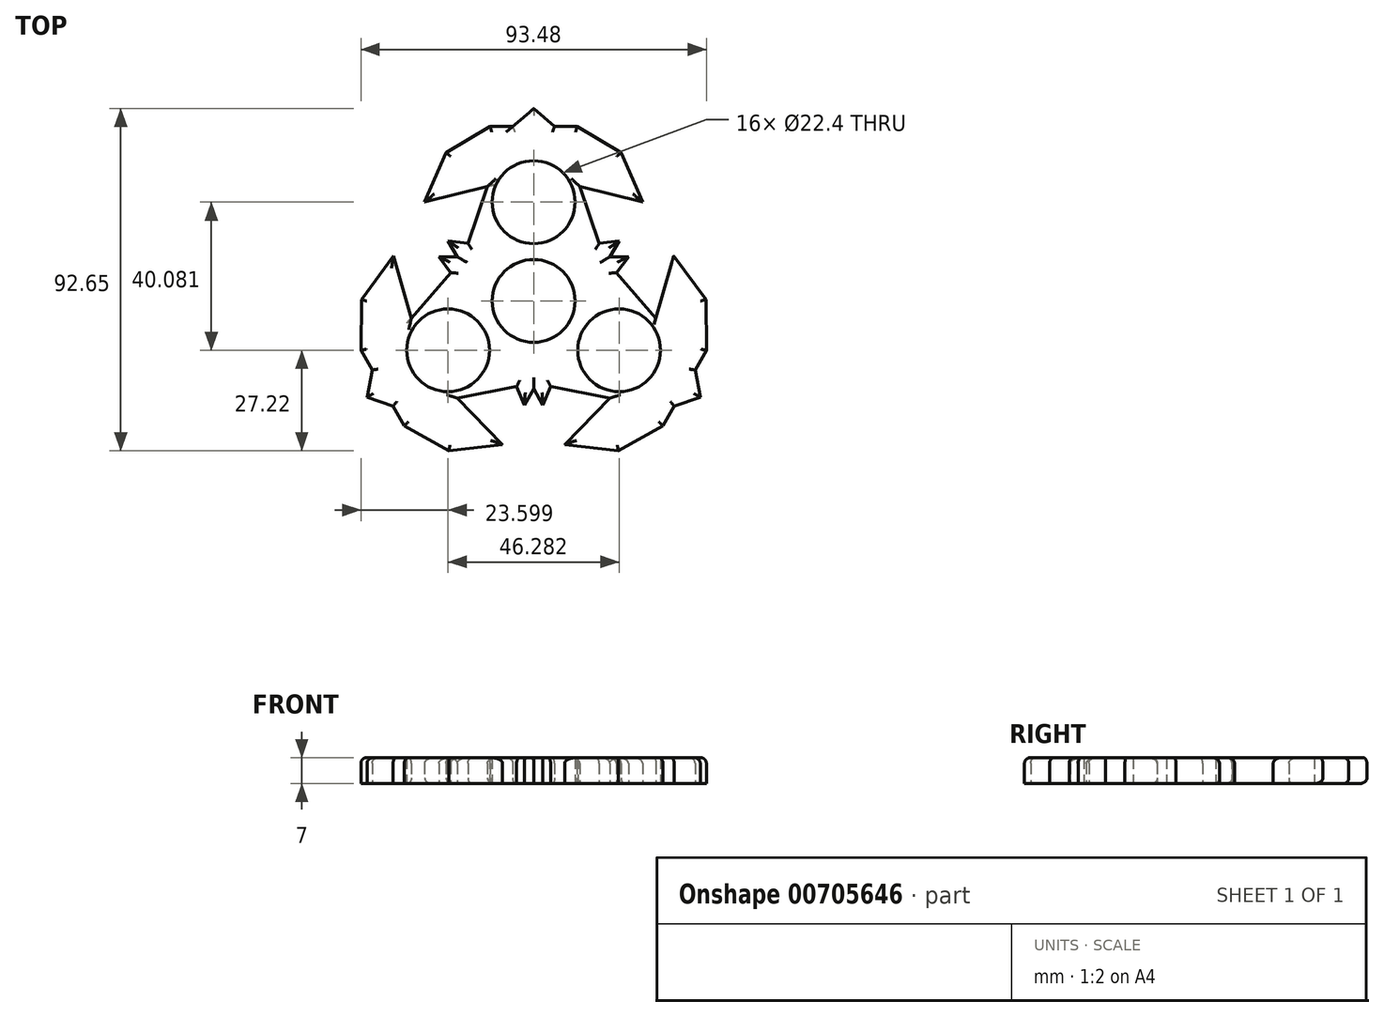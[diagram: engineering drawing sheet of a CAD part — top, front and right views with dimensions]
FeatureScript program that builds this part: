
annotation { "Feature Type Name" : "Feature", "Feature Type Description" : "" }
export const myFeature = defineFeature(function(context is Context, id is Id, definition is map)
    precondition{}
    {
        {
            var Q0;
            Q0=qCreatedBy(makeId("Top.planeOp"),FACE);
            var sketch = newSketch(context, id + "F0", { "sketchPlane" : qUnion([Q0])});
            skCircle(sketch, "E0", {"center": v(0, 0) * mm, "radius": 11.2 * mm});
            skCircle(sketch, "E1", {"center": v(0, 26.72) * mm, "radius": 11.2 * mm});
            skLineSegment(sketch, "E2", {"start": v(-12.5, 30.98) * mm, "end": v(-29.47, 26.72) * mm});
            skLineSegment(sketch, "E3", {"start": v(-29.47, 26.72) * mm, "end": v(-23.67, 40.16) * mm});
            skLineSegment(sketch, "E4", {"start": v(-23.67, 40.16) * mm, "end": v(-11.76, 47.18) * mm});
            skLineSegment(sketch, "E5", {"start": v(-11.76, 47.18) * mm, "end": v(-5.65, 47.18) * mm});
            skLineSegment(sketch, "E6", {"start": v(-5.65, 47.18) * mm, "end": v(0, 52.07) * mm});
            skLineSegment(sketch, "E7.MirrorCS", {"start": v(5.65, 47.18) * mm, "end": v(0, 52.07) * mm});
            skLineSegment(sketch, "E8.MirrorCS", {"start": v(11.76, 47.18) * mm, "end": v(5.65, 47.18) * mm});
            skLineSegment(sketch, "E9.MirrorCS", {"start": v(23.67, 40.16) * mm, "end": v(11.76, 47.18) * mm});
            skLineSegment(sketch, "E10.MirrorCS", {"start": v(29.47, 26.72) * mm, "end": v(23.67, 40.16) * mm});
            skLineSegment(sketch, "E11.MirrorCS", {"start": v(12.5, 30.98) * mm, "end": v(29.47, 26.72) * mm});
            skCircle(sketch, "E12.1.1", {"center": v(-23.14, -13.36) * mm, "radius": 11.2 * mm});
            skLineSegment(sketch, "E12.1.2", {"start": v(-43.69, -18.7) * mm, "end": v(-45.1, -26.03) * mm});
            skLineSegment(sketch, "E12.1.3", {"start": v(-38.04, -28.48) * mm, "end": v(-45.1, -26.03) * mm});
            skLineSegment(sketch, "E12.1.4", {"start": v(-46.74, -13.4) * mm, "end": v(-43.69, -18.7) * mm});
            skLineSegment(sketch, "E12.1.5", {"start": v(-34.98, -33.77) * mm, "end": v(-38.04, -28.48) * mm});
            skLineSegment(sketch, "E12.1.6", {"start": v(-22.94, -40.58) * mm, "end": v(-34.98, -33.77) * mm});
            skLineSegment(sketch, "E12.1.7", {"start": v(-46.61, 0.42) * mm, "end": v(-46.74, -13.4) * mm});
            skLineSegment(sketch, "E12.1.8", {"start": v(-8.4, -38.88) * mm, "end": v(-22.94, -40.58) * mm});
            skLineSegment(sketch, "E12.1.9", {"start": v(-37.88, 12.16) * mm, "end": v(-46.61, 0.42) * mm});
            skLineSegment(sketch, "E12.1.10", {"start": v(-33.08, -4.67) * mm, "end": v(-37.88, 12.16) * mm});
            skLineSegment(sketch, "E12.1.11", {"start": v(-20.59, -26.31) * mm, "end": v(-8.4, -38.88) * mm});
            skCircle(sketch, "E12.2.1", {"center": v(23.14, -13.36) * mm, "radius": 11.2 * mm});
            skLineSegment(sketch, "E12.2.2", {"start": v(38.04, -28.48) * mm, "end": v(45.1, -26.03) * mm});
            skLineSegment(sketch, "E12.2.3", {"start": v(43.69, -18.7) * mm, "end": v(45.1, -26.03) * mm});
            skLineSegment(sketch, "E12.2.4", {"start": v(34.98, -33.77) * mm, "end": v(38.04, -28.48) * mm});
            skLineSegment(sketch, "E12.2.5", {"start": v(46.74, -13.4) * mm, "end": v(43.69, -18.7) * mm});
            skLineSegment(sketch, "E12.2.6", {"start": v(46.61, 0.42) * mm, "end": v(46.74, -13.4) * mm});
            skLineSegment(sketch, "E12.2.7", {"start": v(22.94, -40.58) * mm, "end": v(34.98, -33.77) * mm});
            skLineSegment(sketch, "E12.2.8", {"start": v(37.88, 12.16) * mm, "end": v(46.61, 0.42) * mm});
            skLineSegment(sketch, "E12.2.9", {"start": v(8.4, -38.88) * mm, "end": v(22.94, -40.58) * mm});
            skLineSegment(sketch, "E12.2.10", {"start": v(20.59, -26.31) * mm, "end": v(8.4, -38.88) * mm});
            skLineSegment(sketch, "E12.2.11", {"start": v(33.08, -4.67) * mm, "end": v(37.88, 12.16) * mm});
            skLineSegment(sketch, "E13", {"start": v(-12.5, 30.98) * mm, "end": v(-17.75, 15.58) * mm});
            skLineSegment(sketch, "E14", {"start": v(-17.75, 15.58) * mm, "end": v(-23.18, 16.23) * mm});
            skLineSegment(sketch, "E15", {"start": v(-23.18, 16.23) * mm, "end": v(-19.98, 10.8) * mm});
            skLineSegment(sketch, "E16.MirrorCS", {"start": v(12.5, 30.98) * mm, "end": v(17.75, 15.58) * mm});
            skLineSegment(sketch, "E17.MirrorCS", {"start": v(23.18, 16.23) * mm, "end": v(19.98, 10.8) * mm});
            skLineSegment(sketch, "E18.MirrorCS", {"start": v(17.75, 15.58) * mm, "end": v(23.18, 16.23) * mm});
            skLineSegment(sketch, "E19.1.0", {"start": v(-20.59, -26.31) * mm, "end": v(-4.61, -23.16) * mm});
            skLineSegment(sketch, "E19.1.2", {"start": v(-2.47, -28.2) * mm, "end": v(0.63, -22.7) * mm});
            skLineSegment(sketch, "E19.1.3", {"start": v(-4.61, -23.16) * mm, "end": v(-2.47, -28.2) * mm});
            skLineSegment(sketch, "E19.1.5", {"start": v(-25.65, 11.96) * mm, "end": v(-19.34, 11.9) * mm});
            skLineSegment(sketch, "E19.1.6", {"start": v(-22.36, 7.58) * mm, "end": v(-25.65, 11.96) * mm});
            skLineSegment(sketch, "E19.1.7", {"start": v(-33.08, -4.67) * mm, "end": v(-22.36, 7.58) * mm});
            skLineSegment(sketch, "E19.2.0", {"start": v(33.08, -4.67) * mm, "end": v(22.36, 7.58) * mm});
            skLineSegment(sketch, "E19.2.2", {"start": v(25.65, 11.96) * mm, "end": v(20.63, 11.91) * mm});
            skLineSegment(sketch, "E19.2.3", {"start": v(22.36, 7.58) * mm, "end": v(25.65, 11.96) * mm});
            skLineSegment(sketch, "E19.2.5", {"start": v(2.47, -28.2) * mm, "end": v(-0.63, -22.7) * mm});
            skLineSegment(sketch, "E19.2.6", {"start": v(4.61, -23.16) * mm, "end": v(2.47, -28.2) * mm});
            skLineSegment(sketch, "E19.2.7", {"start": v(20.59, -26.31) * mm, "end": v(4.61, -23.16) * mm});
            skSolve(sketch);
        }
        {
            var Q0;
            Q0=makeQuery(id+"F0.imprint","IMPRINT",FACE,{"disambiguationData":[TD([[makeQuery(id+"F0.imprint","IMPRINT",EDGE,{"derivedFrom":sQuery(id+"F0.wireOp",EDGE,"E0")}),-1.0]])]});
            extrude(context, id + "F1", {"entities" : qUnion([Q0]), "depth" : 7 * mm, "offsetDistance" : 25 * mm});
        }
        {
            var Q0;
            Q0=makeQuery(id+"F1.opExtrude","CAP_EDGE",EDGE,{"disambiguationData":[OSD([sQuery(id+"F0.wireOp",EDGE,"E11.MirrorCS")])],"isStart":false});
            var Q1;
            Q1=makeQuery(id+"F1.opExtrude","CAP_EDGE",EDGE,{"disambiguationData":[OSD([sQuery(id+"F0.wireOp",EDGE,"E10.MirrorCS")])],"isStart":false});
            var Q2;
            Q2=makeQuery(id+"F1.opExtrude","CAP_EDGE",EDGE,{"disambiguationData":[OSD([sQuery(id+"F0.wireOp",EDGE,"E9.MirrorCS")])],"isStart":false});
            var Q3;
            Q3=makeQuery(id+"F1.opExtrude","CAP_EDGE",EDGE,{"disambiguationData":[OSD([sQuery(id+"F0.wireOp",EDGE,"E8.MirrorCS")])],"isStart":false});
            var Q4;
            Q4=makeQuery(id+"F1.opExtrude","CAP_EDGE",EDGE,{"disambiguationData":[OSD([sQuery(id+"F0.wireOp",EDGE,"E7.MirrorCS")])],"isStart":false});
            var Q5;
            Q5=makeQuery(id+"F1.opExtrude","CAP_EDGE",EDGE,{"disambiguationData":[OSD([sQuery(id+"F0.wireOp",EDGE,"E5")])],"isStart":false});
            var Q6;
            Q6=makeQuery(id+"F1.opExtrude","CAP_EDGE",EDGE,{"disambiguationData":[OSD([sQuery(id+"F0.wireOp",EDGE,"E4")])],"isStart":false});
            var Q7;
            Q7=makeQuery(id+"F1.opExtrude","CAP_EDGE",EDGE,{"disambiguationData":[OSD([sQuery(id+"F0.wireOp",EDGE,"E3")])],"isStart":false});
            var Q8;
            Q8=makeQuery(id+"F1.opExtrude","CAP_EDGE",EDGE,{"disambiguationData":[OSD([sQuery(id+"F0.wireOp",EDGE,"E2")])],"isStart":false});
            var Q9;
            Q9=makeQuery(id+"F1.opExtrude","CAP_EDGE",EDGE,{"disambiguationData":[OSD([sQuery(id+"F0.wireOp",EDGE,"E13")])],"isStart":false});
            var Q10;
            Q10=makeQuery(id+"F1.opExtrude","CAP_EDGE",EDGE,{"disambiguationData":[OSD([sQuery(id+"F0.wireOp",EDGE,"E14")])],"isStart":false});
            var Q11;
            Q11=makeQuery(id+"F1.opExtrude","CAP_EDGE",EDGE,{"disambiguationData":[OSD([sQuery(id+"F0.wireOp",EDGE,"E19.1.7")])],"isStart":false});
            var Q12;
            Q12=makeQuery(id+"F1.opExtrude","CAP_EDGE",EDGE,{"disambiguationData":[OSD([sQuery(id+"F0.wireOp",EDGE,"E19.1.5")])],"isStart":false});
            var Q13;
            Q13=makeQuery(id+"F1.opExtrude","CAP_EDGE",EDGE,{"disambiguationData":[OSD([sQuery(id+"F0.wireOp",EDGE,"E15")])],"isStart":false});
            var Q14;
            Q14=makeQuery(id+"F1.opExtrude","CAP_EDGE",EDGE,{"disambiguationData":[OSD([sQuery(id+"F0.wireOp",EDGE,"E19.1.6")])],"isStart":false});
            var Q15;
            Q15=makeQuery(id+"F1.opExtrude","CAP_EDGE",EDGE,{"disambiguationData":[OSD([sQuery(id+"F0.wireOp",EDGE,"E12.1.10")])],"isStart":false});
            var Q16;
            Q16=makeQuery(id+"F1.opExtrude","CAP_EDGE",EDGE,{"disambiguationData":[OSD([sQuery(id+"F0.wireOp",EDGE,"E12.1.9")])],"isStart":false});
            var Q17;
            Q17=makeQuery(id+"F1.opExtrude","CAP_EDGE",EDGE,{"disambiguationData":[OSD([sQuery(id+"F0.wireOp",EDGE,"E12.1.7")])],"isStart":false});
            var Q18;
            Q18=makeQuery(id+"F1.opExtrude","CAP_EDGE",EDGE,{"disambiguationData":[OSD([sQuery(id+"F0.wireOp",EDGE,"E12.1.4")])],"isStart":false});
            var Q19;
            Q19=makeQuery(id+"F1.opExtrude","CAP_EDGE",EDGE,{"disambiguationData":[OSD([sQuery(id+"F0.wireOp",EDGE,"E12.1.2")])],"isStart":false});
            var Q20;
            Q20=makeQuery(id+"F1.opExtrude","CAP_EDGE",EDGE,{"disambiguationData":[OSD([sQuery(id+"F0.wireOp",EDGE,"E12.1.3")])],"isStart":false});
            var Q21;
            Q21=makeQuery(id+"F1.opExtrude","CAP_EDGE",EDGE,{"disambiguationData":[OSD([sQuery(id+"F0.wireOp",EDGE,"E12.1.6")])],"isStart":false});
            var Q22;
            Q22=makeQuery(id+"F1.opExtrude","CAP_EDGE",EDGE,{"disambiguationData":[OSD([sQuery(id+"F0.wireOp",EDGE,"E12.1.8")])],"isStart":false});
            var Q23;
            Q23=makeQuery(id+"F1.opExtrude","CAP_EDGE",EDGE,{"disambiguationData":[OSD([sQuery(id+"F0.wireOp",EDGE,"E12.1.5")])],"isStart":false});
            var Q24;
            Q24=makeQuery(id+"F1.opExtrude","CAP_EDGE",EDGE,{"disambiguationData":[OSD([sQuery(id+"F0.wireOp",EDGE,"E12.1.11")])],"isStart":false});
            var Q25;
            Q25=makeQuery(id+"F1.opExtrude","CAP_EDGE",EDGE,{"disambiguationData":[OSD([sQuery(id+"F0.wireOp",EDGE,"E19.1.0")])],"isStart":false});
            var Q26;
            Q26=makeQuery(id+"F1.opExtrude","CAP_EDGE",EDGE,{"disambiguationData":[OSD([sQuery(id+"F0.wireOp",EDGE,"E19.1.3")])],"isStart":false});
            var Q27;
            Q27=makeQuery(id+"F1.opExtrude","CAP_EDGE",EDGE,{"disambiguationData":[OSD([sQuery(id+"F0.wireOp",EDGE,"E19.2.7")])],"isStart":false});
            var Q28;
            Q28=makeQuery(id+"F1.opExtrude","CAP_EDGE",EDGE,{"disambiguationData":[OSD([sQuery(id+"F0.wireOp",EDGE,"E12.2.10")])],"isStart":false});
            var Q29;
            Q29=makeQuery(id+"F1.opExtrude","CAP_EDGE",EDGE,{"disambiguationData":[OSD([sQuery(id+"F0.wireOp",EDGE,"E19.2.6")])],"isStart":false});
            var Q30;
            Q30=makeQuery(id+"F1.opExtrude","CAP_EDGE",EDGE,{"disambiguationData":[OSD([sQuery(id+"F0.wireOp",EDGE,"E12.2.9")])],"isStart":false});
            var Q31;
            Q31=makeQuery(id+"F1.opExtrude","CAP_EDGE",EDGE,{"disambiguationData":[OSD([sQuery(id+"F0.wireOp",EDGE,"E19.1.2")])],"isStart":false});
            var Q32;
            Q32=makeQuery(id+"F1.opExtrude","CAP_EDGE",EDGE,{"disambiguationData":[OSD([sQuery(id+"F0.wireOp",EDGE,"E19.2.5")])],"isStart":false});
            var Q33;
            Q33=makeQuery(id+"F1.opExtrude","CAP_EDGE",EDGE,{"disambiguationData":[OSD([sQuery(id+"F0.wireOp",EDGE,"E12.2.7")])],"isStart":false});
            var Q34;
            Q34=makeQuery(id+"F1.opExtrude","CAP_EDGE",EDGE,{"disambiguationData":[OSD([sQuery(id+"F0.wireOp",EDGE,"E12.2.4")])],"isStart":false});
            var Q35;
            Q35=makeQuery(id+"F1.opExtrude","CAP_EDGE",EDGE,{"disambiguationData":[OSD([sQuery(id+"F0.wireOp",EDGE,"E12.2.2")])],"isStart":false});
            var Q36;
            Q36=makeQuery(id+"F1.opExtrude","CAP_EDGE",EDGE,{"disambiguationData":[OSD([sQuery(id+"F0.wireOp",EDGE,"E12.2.3")])],"isStart":false});
            var Q37;
            Q37=makeQuery(id+"F1.opExtrude","CAP_EDGE",EDGE,{"disambiguationData":[OSD([sQuery(id+"F0.wireOp",EDGE,"E12.2.5")])],"isStart":false});
            var Q38;
            Q38=makeQuery(id+"F1.opExtrude","CAP_EDGE",EDGE,{"disambiguationData":[OSD([sQuery(id+"F0.wireOp",EDGE,"E12.2.6")])],"isStart":false});
            var Q39;
            Q39=makeQuery(id+"F1.opExtrude","CAP_EDGE",EDGE,{"disambiguationData":[OSD([sQuery(id+"F0.wireOp",EDGE,"E12.2.8")])],"isStart":false});
            var Q40;
            Q40=makeQuery(id+"F1.opExtrude","CAP_EDGE",EDGE,{"disambiguationData":[OSD([sQuery(id+"F0.wireOp",EDGE,"E19.2.0")])],"isStart":false});
            var Q41;
            Q41=makeQuery(id+"F1.opExtrude","CAP_EDGE",EDGE,{"disambiguationData":[OSD([sQuery(id+"F0.wireOp",EDGE,"E19.2.3")])],"isStart":false});
            var Q42;
            Q42=makeQuery(id+"F1.opExtrude","CAP_EDGE",EDGE,{"disambiguationData":[OSD([sQuery(id+"F0.wireOp",EDGE,"E18.MirrorCS")])],"isStart":false});
            var Q43;
            Q43=makeQuery(id+"F1.opExtrude","CAP_EDGE",EDGE,{"disambiguationData":[OSD([sQuery(id+"F0.wireOp",EDGE,"E16.MirrorCS")])],"isStart":false});
            var Q44;
            Q44=makeQuery(id+"F1.opExtrude","CAP_EDGE",EDGE,{"disambiguationData":[OSD([sQuery(id+"F0.wireOp",EDGE,"E19.2.2")])],"isStart":false});
            var Q45;
            Q45=makeQuery(id+"F1.opExtrude","CAP_EDGE",EDGE,{"disambiguationData":[OSD([sQuery(id+"F0.wireOp",EDGE,"E17.MirrorCS")])],"isStart":false});
            var Q46;
            Q46=makeQuery(id+"F1.opExtrude","CAP_EDGE",EDGE,{"disambiguationData":[OSD([sQuery(id+"F0.wireOp",EDGE,"E9.MirrorCS")])],"isStart":true});
            var Q47;
            Q47=makeQuery(id+"F1.opExtrude","CAP_EDGE",EDGE,{"disambiguationData":[OSD([sQuery(id+"F0.wireOp",EDGE,"E8.MirrorCS")])],"isStart":true});
            var Q48;
            Q48=makeQuery(id+"F1.opExtrude","CAP_EDGE",EDGE,{"disambiguationData":[OSD([sQuery(id+"F0.wireOp",EDGE,"E7.MirrorCS")])],"isStart":true});
            var Q49;
            Q49=makeQuery(id+"F1.opExtrude","CAP_EDGE",EDGE,{"disambiguationData":[OSD([sQuery(id+"F0.wireOp",EDGE,"E5")])],"isStart":true});
            var Q50;
            Q50=makeQuery(id+"F1.opExtrude","CAP_EDGE",EDGE,{"disambiguationData":[OSD([sQuery(id+"F0.wireOp",EDGE,"E4")])],"isStart":true});
            var Q51;
            Q51=makeQuery(id+"F1.opExtrude","CAP_EDGE",EDGE,{"disambiguationData":[OSD([sQuery(id+"F0.wireOp",EDGE,"E6")])],"isStart":true});
            var Q52;
            Q52=makeQuery(id+"F1.opExtrude","CAP_EDGE",EDGE,{"disambiguationData":[OSD([sQuery(id+"F0.wireOp",EDGE,"E3")])],"isStart":true});
            var Q53;
            Q53=makeQuery(id+"F1.opExtrude","CAP_EDGE",EDGE,{"disambiguationData":[OSD([sQuery(id+"F0.wireOp",EDGE,"E13")])],"isStart":true});
            var Q54;
            Q54=makeQuery(id+"F1.opExtrude","CAP_EDGE",EDGE,{"disambiguationData":[OSD([sQuery(id+"F0.wireOp",EDGE,"E14")])],"isStart":true});
            var Q55;
            Q55=makeQuery(id+"F1.opExtrude","CAP_EDGE",EDGE,{"disambiguationData":[OSD([sQuery(id+"F0.wireOp",EDGE,"E12.1.10")])],"isStart":true});
            fillet(context, id + "F2", {"entities" : qUnion([Q0, Q1, Q2, Q3, Q4, Q5, Q6, Q7, Q8, Q9, Q10, Q11, Q12, Q13, Q14, Q15, Q16, Q17, Q18, Q19, Q20, Q21, Q22, Q23, Q24, Q25, Q26, Q27, Q28, Q29, Q30, Q31, Q32, Q33, Q34, Q35, Q36, Q37, Q38, Q39, Q40, Q41, Q42, Q43, Q44, Q45, Q46, Q47, Q48, Q49, Q50, Q51, Q52, Q53, Q54, Q55]), "radius" : 1.5 * mm, "tangentPropagation" : true, "allowEdgeOverflow" : false});
        }
    });
